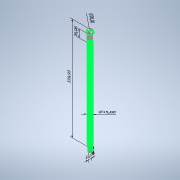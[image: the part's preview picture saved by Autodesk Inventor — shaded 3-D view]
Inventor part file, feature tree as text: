
AUTODESK INVENTOR PART (.ipt)
format: ipt  version: 2021 (Build 250183000, 183)  size: 3,041,792 bytes
history: native  units: mm
features: sketch x11, other x7, extrude x7, thicken_offset x7, revolve x2, helix x2
ambient origin geometry x8: Origin, YZ Plane, XZ Plane, XY Plane, X Axis, Y Axis, Z Axis, Center Point
bodies: Solid1 (feature_tree)
feature tree (36):
  other  "Annotations"
  extrude  "Extrusion1"  Depth=350.0mm TaperAngle=0.0deg
  revolve  "Revolution1"  [1 undecoded]
  extrude  "Extrusion2"  Depth=20.0mm TaperAngle=0.0deg
  extrude  "Extrusion3"  Depth=10.0mm
  revolve  "Revolution2"  Angle=90.0deg
  thicken_offset  "Thicken1"
  thicken_offset  "Thicken2"
  thicken_offset  "Thicken3"
  thicken_offset  "Thicken4"
  thicken_offset  "Thicken5"
  thicken_offset  "Thicken6"
  thicken_offset  "Thicken7"
  helix  "Coil1"  [1 undecoded]
  extrude  "Extrusion4"  Depth=10.0mm
  extrude  "Extrusion5"  Depth=10.0mm
  helix  "Coil2"  [1 undecoded]
  extrude  "Extrusion6"  Depth=10.0mm
  extrude  "Extrusion7"  Depth=10.0mm
  sketch  "Sketch1"  dims[d0=15.0mm d1=350.0mm d2=0.0mm]
  sketch  "Sketch2"  dims[d3=15.0mm d4=9.0mm]
  sketch  "Sketch3"  dims[d5=90.0deg d6=20.0mm d7=0.0mm]
  sketch  "Sketch4"  dims[d14=30.0mm d15=0.0mm d16=10.0mm]
  sketch  "Sketch5"  dims[d17=20.0mm d18=90.0deg d19=10.0mm]
  sketch  "Sketch6"  dims[d20=10.0mm d21=10.0mm]
  sketch  "Sketch7"  dims[d22=10.0mm d23=10.0mm d24=10.0mm]
  sketch  "Sketch8"  dims[d25=10.0mm d26=10.0mm]
  sketch  "Sketch9"  dims[d27=10.0mm d28=10.0mm]
  sketch  "Sketch10"  dims[d29=10.0mm]
  sketch  "Sketch11"  dims[d30=10.0mm d31=10.0mm d32=10.0mm d36=20.0mm d38=1.22686mm d39=2.0mm d40=0.28868mm d41=1.0mm d46=2.0mm d47=10.0mm d48=1570.0mm d49=0.0mm d50=90.0deg d51=90.0deg d52=0.0mm d53=0.0mm d54=15.0mm d55=340.0mm d56=0.0mm d57=20.0mm d58=0.0mm d60=1.22686mm d61=0.28868mm d62=60.0deg d63=60.0deg d64=2.0mm d65=10.0mm d66=1570.0mm d67=0.0mm d68=90.0deg d69=90.0deg d70=0.0mm d71=0.0mm d72=15.0mm d73=20.0mm d74=0.0mm d75=6.0mm d76=20.0mm d77=0.0mm d10=7.805911mm d11=15.0mm d78=9.484691mm d79=4.612622mm d8=40.227195mm d80=339.934981mm d81=0.0mm d82=10.0mm d83=20.0mm d84=26.060409mm d85=39.531131mm d86=20.0mm d87=12.0mm d9=2.677461mm]
  other  "Diameter Dimension 1"
  other  "Linear Dimension 1"
  other  "Linear Dimension 2"
  other  "Linear Dimension 3"
  other  "Diameter Dimension 2"
  other  "Linear Dimension 4"
note: 3 required parameter values undecoded (feature->parameter linkage not recoverable at this tier; creation-order binding heuristic only, values carry confidence <= 0.55)